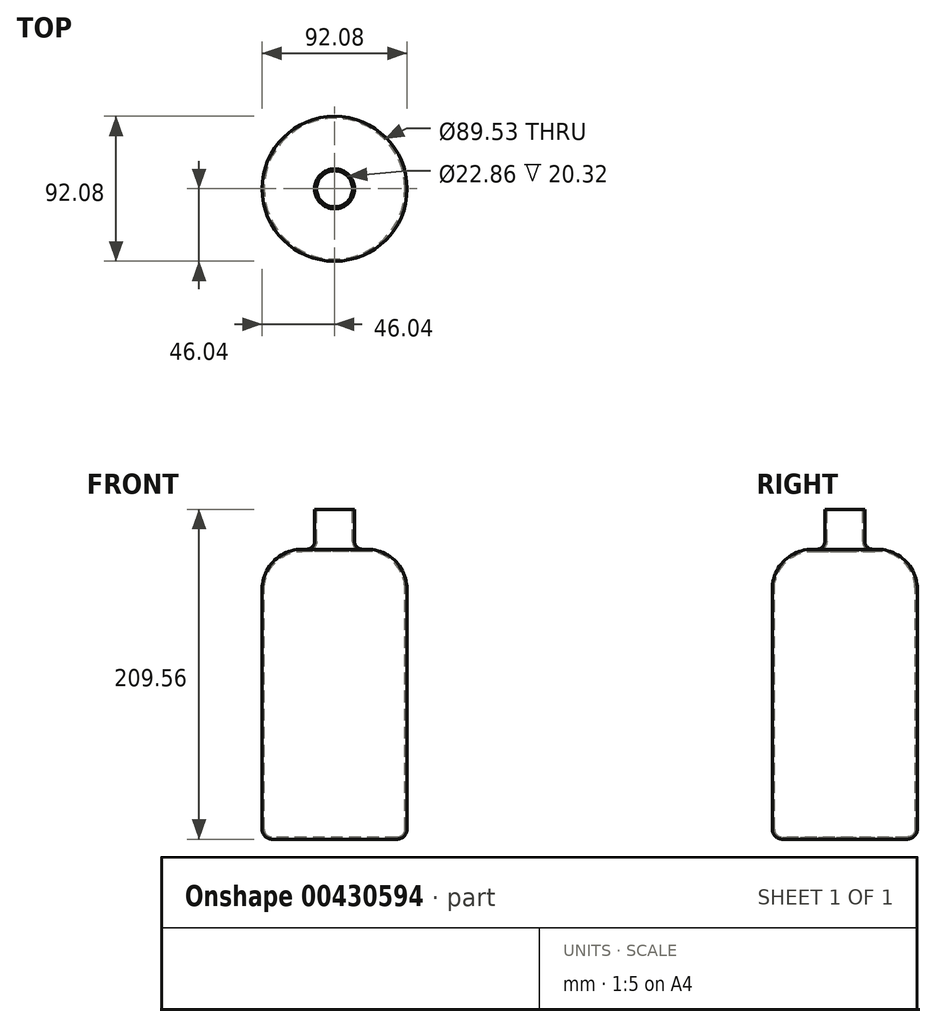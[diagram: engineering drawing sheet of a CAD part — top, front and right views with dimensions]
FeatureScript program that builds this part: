
annotation { "Feature Type Name" : "Feature", "Feature Type Description" : "" }
export const myFeature = defineFeature(function(context is Context, id is Id, definition is map)
    precondition{}
    {
        {
            var Q0;
            Q0=qCreatedBy(makeId("Front.planeOp"),FACE);
            var sketch = newSketch(context, id + "F0", { "sketchPlane" : qUnion([Q0])});
            skLineSegment(sketch, "E0.bottom", {"start": v(0, -104.78) * mm, "end": v(-39.69, -104.78) * mm});
            skLineSegment(sketch, "E0.top", {"start": v(-11.43, 104.78) * mm, "end": v(-12.7, 104.78) * mm});
            skLineSegment(sketch, "E0.right", {"start": v(-46.04, -98.43) * mm, "end": v(-46.04, 53.97) * mm});
            skPoint(sketch, "E0.middle", {"position": v(0, 0) * mm});
            skLineSegment(sketch, "E1", {"start": v(0, 104.78) * mm, "end": v(0, -104.78) * mm});
            skPoint(sketch, "E2.visualSharp", {"position": v(-46.04, -104.78) * mm});
            skArc(sketch, "E2.filletArc", {"start": v(-46.04, -98.43) * mm, "mid": v(-44.18, -102.92) * mm, "end": v(-39.69, -104.78) * mm});
            skLineSegment(sketch, "E3", {"start": v(-17.78, 79.37) * mm, "end": v(-20.64, 79.37) * mm});
            skArc(sketch, "E4.filletArc", {"start": v(-20.64, 79.38) * mm, "mid": v(-38.6, 71.94) * mm, "end": v(-46.04, 53.97) * mm});
            skPoint(sketch, "E5.visualSharp", {"position": v(-12.7, 79.38) * mm});
            skLineSegment(sketch, "E6", {"start": v(-12.7, 84.45) * mm, "end": v(-12.7, 104.78) * mm});
            skPoint(sketch, "E7.visualSharp", {"position": v(-12.7, 79.37) * mm});
            skArc(sketch, "E7.filletArc", {"start": v(-17.78, 79.38) * mm, "mid": v(-14.19, 80.86) * mm, "end": v(-12.7, 84.45) * mm});
            skLineSegment(sketch, "E8.0", {"start": v(-11.43, 84.45) * mm, "end": v(-11.43, 104.78) * mm});
            skArc(sketch, "E8.1", {"start": v(-17.78, 78.1) * mm, "mid": v(-13.29, 79.96) * mm, "end": v(-11.43, 84.45) * mm});
            skLineSegment(sketch, "E8.2", {"start": v(0, -103.5) * mm, "end": v(-39.69, -103.5) * mm});
            skLineSegment(sketch, "E8.3", {"start": v(-44.77, -98.43) * mm, "end": v(-44.77, 53.97) * mm});
            skArc(sketch, "E8.4", {"start": v(-20.64, 78.1) * mm, "mid": v(-37.7, 71.04) * mm, "end": v(-44.77, 53.97) * mm});
            skLineSegment(sketch, "E8.5", {"start": v(-17.78, 78.1) * mm, "end": v(-20.64, 78.1) * mm});
            skPoint(sketch, "E9.visualSharp", {"position": v(-44.77, -103.5) * mm});
            skArc(sketch, "E9.filletArc", {"start": v(-44.77, -98.43) * mm, "mid": v(-43.28, -102.02) * mm, "end": v(-39.69, -103.5) * mm});
            skSolve(sketch);
        }
        {
            var Q0;
            Q0 = qSketchRegion(id + "F0", true);
            var Q1;
            Q1=sQuery(id+"F0.wireOp",EDGE,"E1");
            revolve(context, id + "F1", {"entities" : qUnion([Q0]), "axis" : qUnion([Q1]), "revolveType" : RevolveType.FULL});
        }
    });
